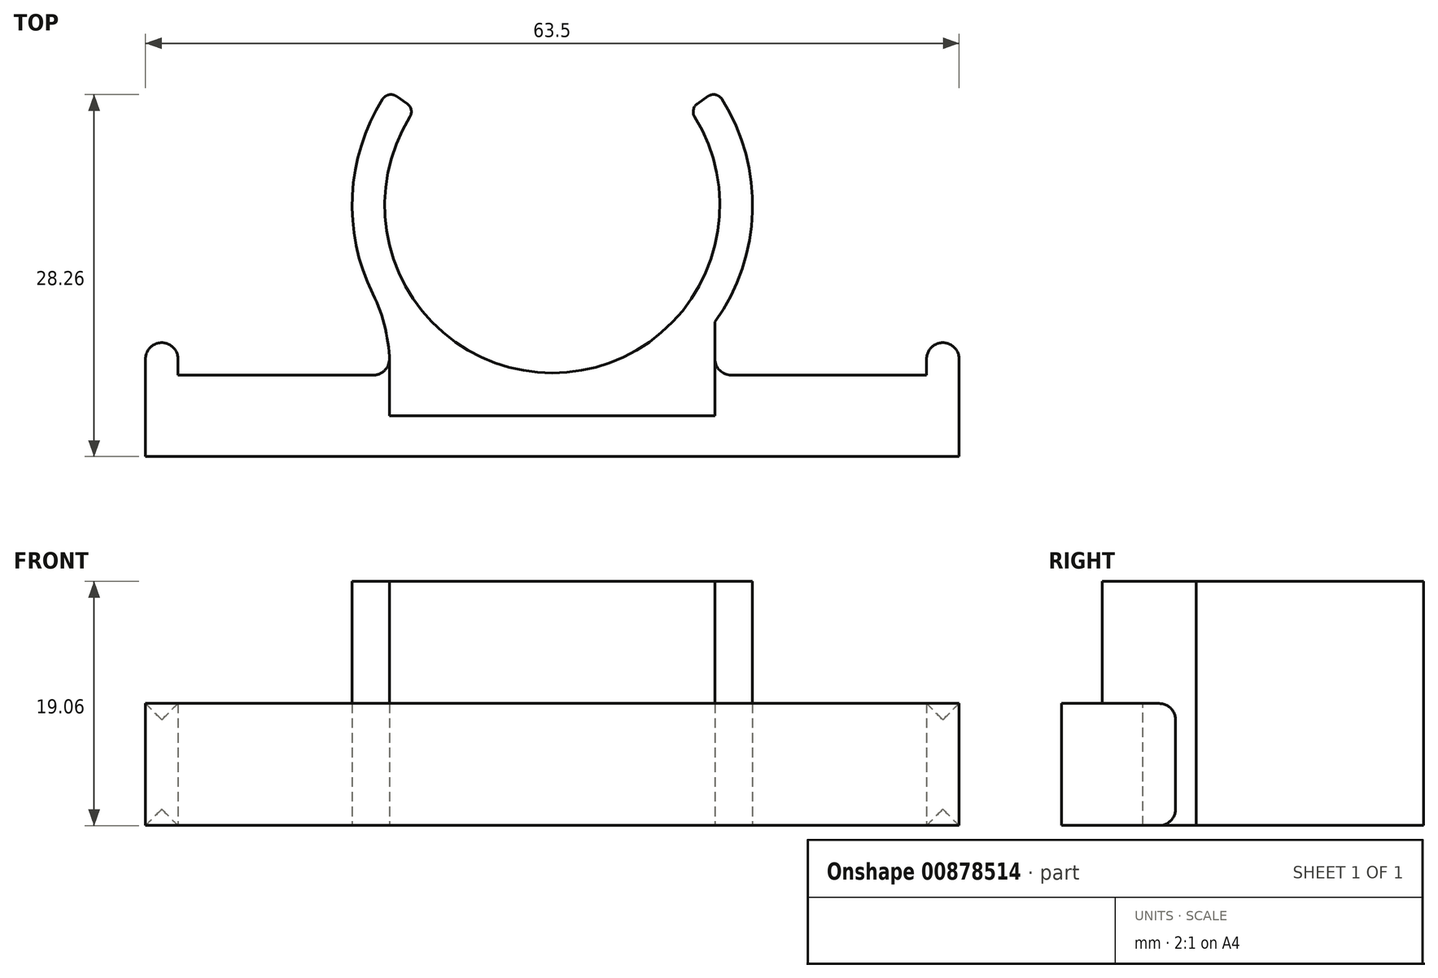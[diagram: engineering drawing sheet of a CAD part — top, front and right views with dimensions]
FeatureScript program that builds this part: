
annotation { "Feature Type Name" : "Feature", "Feature Type Description" : "" }
export const myFeature = defineFeature(function(context is Context, id is Id, definition is map)
    precondition{}
    {
        {
            var Q0;
            Q0=qCreatedBy(makeId("Top.planeOp"),FACE);
            var sketch = newSketch(context, id + "F0", { "sketchPlane" : qUnion([Q0])});
            skCircle(sketch, "E0", {"center": v(0, 0) * mm, "radius": 15.62 * mm});
            skCircle(sketch, "E1", {"center": v(0, 0) * mm, "radius": 13.08 * mm});
            skLineSegment(sketch, "E2", {"start": v(-53.94, 0) * mm, "end": v(51.47, 0) * mm, "construction": true});
            skLineSegment(sketch, "E3", {"start": v(0, 37.95) * mm, "end": v(0, -48.77) * mm, "construction": true});
            skLineSegment(sketch, "E4", {"start": v(0, 0) * mm, "end": v(-12.8, 8.96) * mm});
            skLineSegment(sketch, "E5.MirrorCS", {"start": v(0, 0) * mm, "end": v(12.8, 8.96) * mm});
            skLineSegment(sketch, "E6.top", {"start": v(-12.7, -16.43) * mm, "end": v(12.7, -16.43) * mm});
            skLineSegment(sketch, "E6.left", {"start": v(-12.7, -9.1) * mm, "end": v(-12.7, -16.43) * mm});
            skLineSegment(sketch, "E6.right", {"start": v(12.7, -9.1) * mm, "end": v(12.7, -16.43) * mm});
            skPoint(sketch, "E6.middle", {"position": v(0, -12.76) * mm});
            skCircle(sketch, "E7", {"center": v(0, 0) * mm, "radius": 13.34 * mm, "construction": true});
            skSolve(sketch);
        }
        {
            var Q0;
            {var subQ0=sQuery(id+"F0.wireOp",EDGE,"E4");var subQ5=sQuery(id+"F0.wireOp",EDGE,"E0");var subQ9=makeQuery(id+"F0.imprint","INTERSECT",VERTEX,{"derivedFrom":[subQ5,subQ0]});Q0=makeQuery(id+"F0.imprint","IMPRINT",FACE,{"disambiguationData":[TD([[makeQuery(id+"F0.imprint","IMPRINT",EDGE,{"disambiguationData":[TD([[subQ9,-1.0]])],"derivedFrom":subQ5}),1.0]])]});}
            extrude(context, id + "F1", {"entities" : qUnion([Q0]), "endBound" : BoundingType.SYMMETRIC, "depth" : 19.05 * mm, "offsetDistance" : 25.4 * mm});
        }
        {
            var Q0;
            Q0=makeQuery(id+"F0.imprint","IMPRINT",FACE,{"disambiguationData":[TD([[makeQuery(id+"F0.imprint","IMPRINT",EDGE,{"derivedFrom":sQuery(id+"F0.wireOp",EDGE,"E6.top")}),1.0]])]});
            extrude(context, id + "F2", {"entities" : qUnion([Q0]), "operationType" : NewBodyOperationType.ADD, "endBound" : BoundingType.SYMMETRIC, "depth" : 19.05 * mm, "offsetDistance" : 25.4 * mm});
        }
        {
            var Q0;
            Q0=makeQuery(id+"F2.opExtrude","SWEPT_EDGE",EDGE,{"disambiguationData":[OSD([sQuery(id+"F0.wireOp",EDGE,"E0"),sQuery(id+"F0.wireOp",EDGE,"E6.left")])]});
            var Q1;
            Q1=makeQuery(id+"F2.opExtrude","SWEPT_EDGE",EDGE,{"disambiguationData":[OSD([sQuery(id+"F0.wireOp",EDGE,"E0"),sQuery(id+"F0.wireOp",EDGE,"E6.right")])]});
            fillet(context, id + "F3", {"entities" : qUnion([Q0, Q1]), "radius" : 12.7 * mm, "tangentPropagation" : true, "allowEdgeOverflow" : false});
        }
        {
            var Q0;
            Q0=makeQuery(id+"F1.opExtrude","SWEPT_EDGE",EDGE,{"disambiguationData":[OSD([sQuery(id+"F0.wireOp",EDGE,"E0"),sQuery(id+"F0.wireOp",EDGE,"E4")])]});
            var Q1;
            Q1=makeQuery(id+"F1.opExtrude","SWEPT_EDGE",EDGE,{"disambiguationData":[OSD([sQuery(id+"F0.wireOp",EDGE,"E1"),sQuery(id+"F0.wireOp",EDGE,"E4")])]});
            var Q2;
            Q2=makeQuery(id+"F1.opExtrude","SWEPT_EDGE",EDGE,{"disambiguationData":[OSD([sQuery(id+"F0.wireOp",EDGE,"E0"),sQuery(id+"F0.wireOp",EDGE,"E5.MirrorCS")])]});
            var Q3;
            Q3=makeQuery(id+"F1.opExtrude","SWEPT_EDGE",EDGE,{"disambiguationData":[OSD([sQuery(id+"F0.wireOp",EDGE,"E1"),sQuery(id+"F0.wireOp",EDGE,"E5.MirrorCS")])]});
            fillet(context, id + "F4", {"entities" : qUnion([Q0, Q1, Q2, Q3]), "radius" : 0.76 * mm, "tangentPropagation" : true, "allowEdgeOverflow" : false});
        }
        {
            var Q0;
            Q0=makeQuery(id+"F2.opExtrude","SWEPT_FACE",FACE,{"disambiguationData":[OSD([sQuery(id+"F0.wireOp",EDGE,"E6.top")])]});
            var sketch = newSketch(context, id + "F5", { "sketchPlane" : qUnion([Q0])});
            skLineSegment(sketch, "E8", {"start": v(0, 13.41) * mm, "end": v(0, -11.32) * mm, "construction": true});
            skLineSegment(sketch, "E9", {"start": v(-20.91, -9.53) * mm, "end": v(24.77, -9.53) * mm, "construction": true});
            skLineSegment(sketch, "E10.bottom", {"start": v(-12.7, 0) * mm, "end": v(12.7, 0) * mm});
            skLineSegment(sketch, "E10.top", {"start": v(-12.7, -9.53) * mm, "end": v(12.7, -9.53) * mm});
            skLineSegment(sketch, "E10.left", {"start": v(-12.7, 0) * mm, "end": v(-12.7, -9.53) * mm});
            skLineSegment(sketch, "E10.right", {"start": v(12.7, 0) * mm, "end": v(12.7, -9.53) * mm});
            skLineSegment(sketch, "E11", {"start": v(-10.16, 0) * mm, "end": v(-10.16, -6.99) * mm});
            skLineSegment(sketch, "E12", {"start": v(-10.16, -6.99) * mm, "end": v(0, -6.99) * mm});
            skLineSegment(sketch, "E13.MirrorCS", {"start": v(10.16, 0) * mm, "end": v(10.16, -6.98) * mm});
            skLineSegment(sketch, "E14.MirrorCS", {"start": v(10.16, -6.98) * mm, "end": v(0, -6.99) * mm});
            skSolve(sketch);
        }
        {
            var Q0;
            {var subQ1=sQuery(id+"F0.wireOp",EDGE,"E6.top");var subQ6=makeQuery(id+"F2.opExtrude","CAP_EDGE",EDGE,{"disambiguationData":[OSD([subQ1])],"isStart":false});Q0=makeQuery(id+"F5.imprint","IMPRINT",FACE,{"disambiguationData":[TD([[makeQuery(id+"F5.imprint","IMPRINT",EDGE,{"derivedFrom":subQ6}),-1.0]])]});}
            var sketch = newSketch(context, id + "F6", { "sketchPlane" : qUnion([Q0])});
            skLineSegment(sketch, "E15", {"start": v(0, 5.75) * mm, "end": v(0, -9.53) * mm, "construction": true});
            skLineSegment(sketch, "E16.bottom", {"start": v(-12.7, -3.22) * mm, "end": v(12.7, -3.22) * mm});
            skLineSegment(sketch, "E16.top", {"start": v(-12.7, -9.53) * mm, "end": v(12.7, -9.53) * mm});
            skLineSegment(sketch, "E16.left", {"start": v(-12.7, -3.22) * mm, "end": v(-12.7, -9.53) * mm});
            skLineSegment(sketch, "E16.right", {"start": v(12.7, -3.22) * mm, "end": v(12.7, -9.53) * mm});
            skLineSegment(sketch, "E17.bottom", {"start": v(-31.75, 0) * mm, "end": v(31.75, 0) * mm});
            skLineSegment(sketch, "E17.top", {"start": v(-31.75, -9.53) * mm, "end": v(31.75, -9.52) * mm});
            skLineSegment(sketch, "E17.left", {"start": v(-31.75, 0) * mm, "end": v(-31.75, -9.53) * mm});
            skLineSegment(sketch, "E17.right", {"start": v(31.75, 0) * mm, "end": v(31.75, -9.52) * mm});
            skSolve(sketch);
        }
        {
            var Q0;
            Q0 = qSketchRegion(id + "F6", true);
            extrude(context, id + "F7", {"entities" : qUnion([Q0]), "operationType" : NewBodyOperationType.ADD, "endBound" : BoundingType.SYMMETRIC, "depth" : 6.35 * mm, "offsetDistance" : 25.4 * mm});
        }
        {
            var Q0;
            {var subQ3=sQuery(id+"F0.wireOp",EDGE,"E6.right");var subQ5=sQuery(id+"F6.wireOp",EDGE,"E17.right");var subQ7=sQuery(id+"F6.wireOp",EDGE,"E17.bottom");var subQ8=sQuery(id+"F6.wireOp",EDGE,"E17.top");Q0=makeQuery(id+"F7.boolean.opBoolean","SPLIT",FACE,{"disambiguationData":[TD([makeQuery(id+"F2.opExtrude","SWEPT_FACE",FACE,{"disambiguationData":[OSD([subQ3])]})])],"derivedFrom":makeQuery(id+"F7.opExtrude","CAP_FACE",FACE,{"disambiguationData":[OSD([subQ7,subQ8,sQuery(id+"F6.wireOp",EDGE,"E17.left"),subQ5])],"isStart":true})});}
            var sketch = newSketch(context, id + "F8", { "sketchPlane" : qUnion([Q0])});
            skLineSegment(sketch, "E18.bottom", {"start": v(-31.75, 0) * mm, "end": v(-29.21, 0) * mm});
            skLineSegment(sketch, "E18.top", {"start": v(-31.75, -9.53) * mm, "end": v(-29.21, -9.53) * mm});
            skLineSegment(sketch, "E18.left", {"start": v(-31.75, 0) * mm, "end": v(-31.75, -9.53) * mm});
            skLineSegment(sketch, "E18.right", {"start": v(-29.21, 0) * mm, "end": v(-29.21, -9.53) * mm});
            skLineSegment(sketch, "E19", {"start": v(0, 16.62) * mm, "end": v(0, -24.22) * mm, "construction": true});
            skLineSegment(sketch, "E20.MirrorCS", {"start": v(31.75, 0) * mm, "end": v(29.21, 0) * mm});
            skLineSegment(sketch, "E21.MirrorCS", {"start": v(31.75, -9.53) * mm, "end": v(29.21, -9.53) * mm});
            skLineSegment(sketch, "E22.MirrorCS", {"start": v(29.21, 0) * mm, "end": v(29.21, -9.52) * mm});
            skLineSegment(sketch, "E23.MirrorCS", {"start": v(31.75, 0) * mm, "end": v(31.75, -9.53) * mm});
            skSolve(sketch);
        }
        {
            var Q0;
            Q0 = qSketchRegion(id + "F8", true);
            extrude(context, id + "F9", {"entities" : qUnion([Q0]), "operationType" : NewBodyOperationType.ADD, "depth" : 2.54 * mm, "offsetDistance" : 25.4 * mm});
        }
        {
            var Q0;
            Q0=makeQuery(id+"FMGU35oFkzE1BuC_1.opExtrude","SWEPT_FACE",FACE,{"disambiguationData":[OSD([sQuery(id+"F5.wireOp",EDGE,"E12"),sQuery(id+"F5.wireOp",EDGE,"E14.MirrorCS")])]});
            var Q1;
            Q1=makeQuery(id+"F7.boolean.opBoolean","INTERSECT",EDGE,{"derivedFrom":[makeQuery(id+"FMGU35oFkzE1BuC_1.opExtrude","SWEPT_FACE",FACE,{"disambiguationData":[OSD([sQuery(id+"F5.wireOp",EDGE,"E13.MirrorCS")])]}),makeQuery(id+"F7.opExtrude","CAP_FACE",FACE,{"disambiguationData":[OSD([sQuery(id+"F6.wireOp",EDGE,"E17.bottom"),sQuery(id+"F6.wireOp",EDGE,"E17.top"),sQuery(id+"F6.wireOp",EDGE,"E17.left"),sQuery(id+"F6.wireOp",EDGE,"E17.right")])],"isStart":true})]});
            var Q2;
            Q2=makeQuery(id+"F7.boolean.opBoolean","INTERSECT",EDGE,{"derivedFrom":[makeQuery(id+"FMGU35oFkzE1BuC_1.opExtrude","SWEPT_FACE",FACE,{"disambiguationData":[OSD([sQuery(id+"F5.wireOp",EDGE,"E11")])]}),makeQuery(id+"F7.opExtrude","CAP_FACE",FACE,{"disambiguationData":[OSD([sQuery(id+"F6.wireOp",EDGE,"E17.bottom"),sQuery(id+"F6.wireOp",EDGE,"E17.top"),sQuery(id+"F6.wireOp",EDGE,"E17.left"),sQuery(id+"F6.wireOp",EDGE,"E17.right")])],"isStart":true})]});
            var Q3;
            Q3=makeQuery(id+"FMGU35oFkzE1BuC_1.opExtrude","CAP_EDGE",EDGE,{"disambiguationData":[OSD([sQuery(id+"F5.wireOp",EDGE,"E11")])],"isStart":true});
            var Q4;
            Q4=makeQuery(id+"FMGU35oFkzE1BuC_1.opExtrude","CAP_EDGE",EDGE,{"disambiguationData":[OSD([sQuery(id+"F5.wireOp",EDGE,"E13.MirrorCS")])],"isStart":true});
            var Q5;
            Q5=makeQuery(id+"F9.opExtrude","CAP_FACE",FACE,{"disambiguationData":[OSD([sQuery(id+"F8.wireOp",EDGE,"E18.bottom"),sQuery(id+"F8.wireOp",EDGE,"E18.top"),sQuery(id+"F8.wireOp",EDGE,"E18.left"),sQuery(id+"F8.wireOp",EDGE,"E18.right")])],"isStart":false});
            var Q6;
            Q6=makeQuery(id+"F9.opExtrude","CAP_FACE",FACE,{"disambiguationData":[OSD([sQuery(id+"F8.wireOp",EDGE,"E20.MirrorCS"),sQuery(id+"F8.wireOp",EDGE,"E21.MirrorCS"),sQuery(id+"F8.wireOp",EDGE,"E22.MirrorCS"),sQuery(id+"F8.wireOp",EDGE,"E23.MirrorCS")])],"isStart":false});
            var Q7;
            Q7=makeQuery(id+"F9.opExtrude","CAP_EDGE",EDGE,{"disambiguationData":[OSD([sQuery(id+"F8.wireOp",EDGE,"E22.MirrorCS")])],"isStart":true});
            var Q8;
            Q8=makeQuery(id+"F9.opExtrude","CAP_EDGE",EDGE,{"disambiguationData":[OSD([sQuery(id+"F8.wireOp",EDGE,"E18.right")])],"isStart":true});
            var Q9;
            Q9=makeQuery(id+"F7.boolean.opBoolean","INTERSECT",EDGE,{"derivedFrom":[makeQuery(id+"FMGU35oFkzE1BuC_1.boolean.opBoolean","MERGE",FACE,{"derivedFrom":[makeQuery(id+"F2.opExtrude","SWEPT_FACE",FACE,{"disambiguationData":[OSD([sQuery(id+"F0.wireOp",EDGE,"E6.right")])]}),makeQuery(id+"FMGU35oFkzE1BuC_1.opExtrude","SWEPT_FACE",FACE,{"disambiguationData":[OSD([sQuery(id+"F5.wireOp",EDGE,"E10.right")])]})]}),makeQuery(id+"F7.opExtrude","CAP_FACE",FACE,{"disambiguationData":[OSD([sQuery(id+"F6.wireOp",EDGE,"E17.bottom"),sQuery(id+"F6.wireOp",EDGE,"E17.top"),sQuery(id+"F6.wireOp",EDGE,"E17.left"),sQuery(id+"F6.wireOp",EDGE,"E17.right")])],"isStart":true})]});
            var Q10;
            Q10=makeQuery(id+"F7.boolean.opBoolean","INTERSECT",EDGE,{"derivedFrom":[makeQuery(id+"FMGU35oFkzE1BuC_1.boolean.opBoolean","MERGE",FACE,{"derivedFrom":[makeQuery(id+"F2.opExtrude","SWEPT_FACE",FACE,{"disambiguationData":[OSD([sQuery(id+"F0.wireOp",EDGE,"E6.left")])]}),makeQuery(id+"FMGU35oFkzE1BuC_1.opExtrude","SWEPT_FACE",FACE,{"disambiguationData":[OSD([sQuery(id+"F5.wireOp",EDGE,"E10.left")])]})]}),makeQuery(id+"F7.opExtrude","CAP_FACE",FACE,{"disambiguationData":[OSD([sQuery(id+"F6.wireOp",EDGE,"E17.bottom"),sQuery(id+"F6.wireOp",EDGE,"E17.top"),sQuery(id+"F6.wireOp",EDGE,"E17.left"),sQuery(id+"F6.wireOp",EDGE,"E17.right")])],"isStart":true})]});
            fillet(context, id + "F10", {"entities" : qUnion([Q0, Q1, Q2, Q3, Q4, Q5, Q6, Q7, Q8, Q9, Q10]), "tangentPropagation" : true, "radius" : 1.27 * mm, "defaultsChanged" : false, "vertexSettings" : [], "allowEdgeOverflow" : false});
        }
    });
